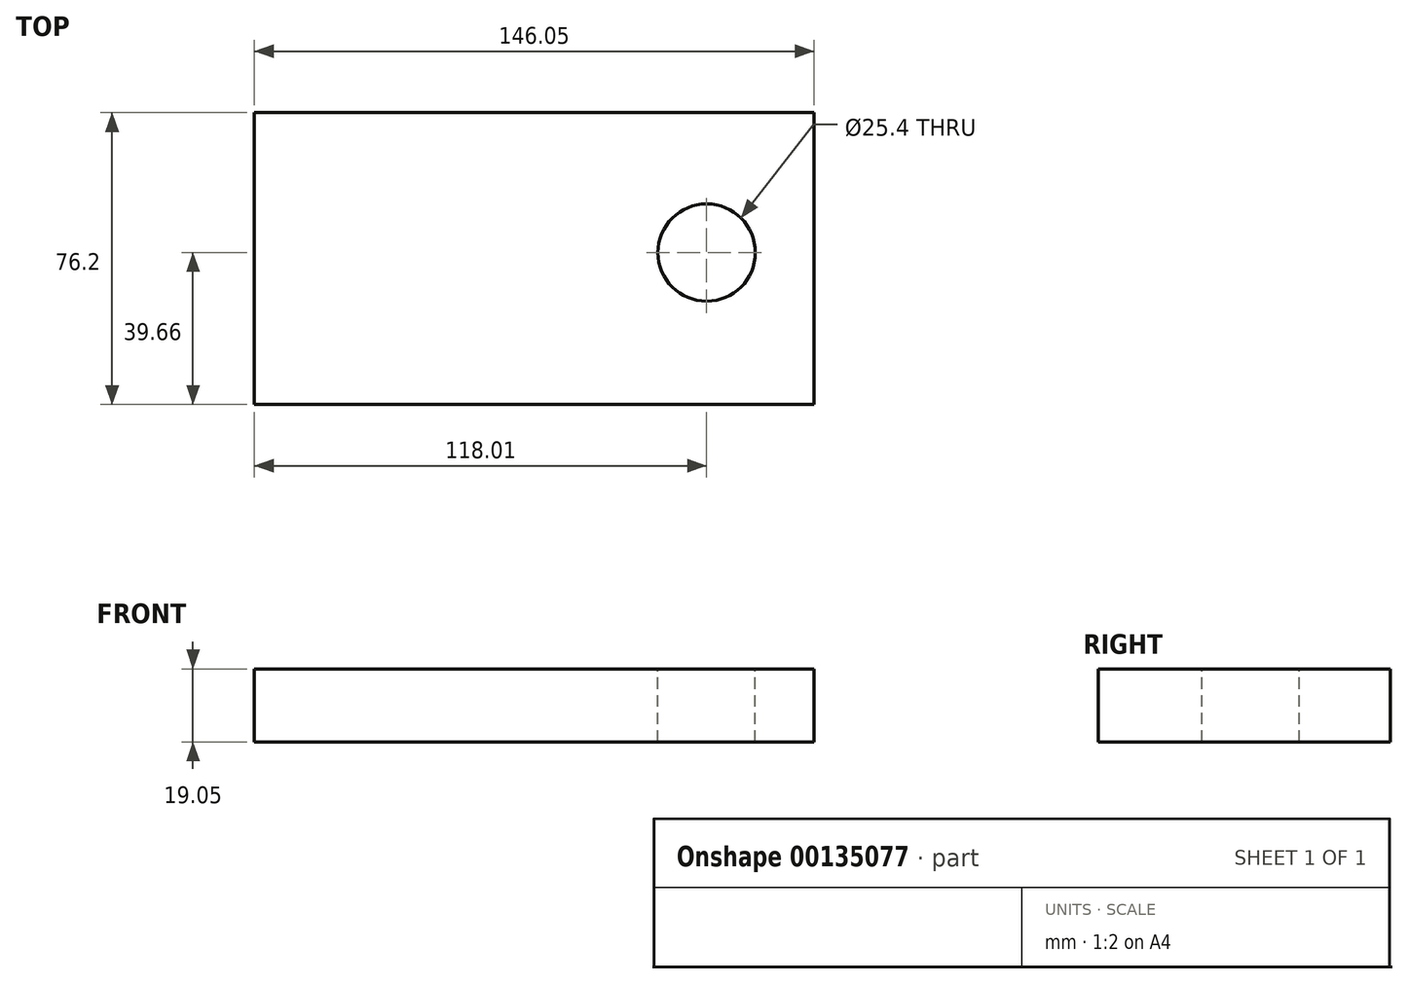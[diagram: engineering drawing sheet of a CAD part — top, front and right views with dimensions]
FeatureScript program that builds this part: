
annotation { "Feature Type Name" : "Feature", "Feature Type Description" : "" }
export const myFeature = defineFeature(function(context is Context, id is Id, definition is map)
    precondition{}
    {
        {
            var Q0;
            Q0=qCreatedBy(makeId("Top.planeOp"),FACE);
            var sketch = newSketch(context, id + "F0", { "sketchPlane" : qUnion([Q0])});
            skLineSegment(sketch, "E0.bottom", {"start": v(-70.58, 36.54) * mm, "end": v(75.47, 36.54) * mm});
            skLineSegment(sketch, "E0.top", {"start": v(-70.58, -39.66) * mm, "end": v(75.47, -39.66) * mm});
            skLineSegment(sketch, "E0.left", {"start": v(-70.58, 36.54) * mm, "end": v(-70.58, -39.66) * mm});
            skLineSegment(sketch, "E0.right", {"start": v(75.47, 36.54) * mm, "end": v(75.47, -39.66) * mm});
            skSolve(sketch);
        }
        {
            var Q0;
            Q0=makeQuery(id+"F0.imprint","IMPRINT",FACE,{"disambiguationData":[TD([[makeQuery(id+"F0.imprint","IMPRINT",EDGE,{"derivedFrom":sQuery(id+"F0.wireOp",EDGE,"E0.bottom")}),-1.0]])]});
            extrude(context, id + "F1", {"entities" : qUnion([Q0]), "depth" : 19.05 * mm});
        }
        {
            var Q0;
            Q0=makeQuery(id+"F1.opExtrude","CAP_FACE",FACE,{"disambiguationData":[OSD([sQuery(id+"F0.wireOp",EDGE,"E0.bottom"),sQuery(id+"F0.wireOp",EDGE,"E0.top"),sQuery(id+"F0.wireOp",EDGE,"E0.left"),sQuery(id+"F0.wireOp",EDGE,"E0.right")])],"isStart":false});
            var sketch = newSketch(context, id + "F2", { "sketchPlane" : qUnion([Q0])});
            skLineSegment(sketch, "E1.bottom", {"start": v(-58.81, 11.6) * mm, "end": v(-33.41, 11.6) * mm});
            skLineSegment(sketch, "E1.top", {"start": v(-58.81, -13.8) * mm, "end": v(-33.41, -13.8) * mm});
            skLineSegment(sketch, "E1.left", {"start": v(-58.81, 11.6) * mm, "end": v(-58.81, -13.8) * mm});
            skLineSegment(sketch, "E1.right", {"start": v(-33.41, 11.6) * mm, "end": v(-33.41, -13.8) * mm});
            skCircle(sketch, "E2", {"center": v(47.43, 0) * mm, "radius": 12.7 * mm});
            skLineSegment(sketch, "E3", {"start": v(0, 11.6) * mm, "end": v(-12.7, -10.4) * mm});
            skLineSegment(sketch, "E4", {"start": v(-12.7, -10.4) * mm, "end": v(12.7, -10.4) * mm});
            skLineSegment(sketch, "E5", {"start": v(12.7, -10.4) * mm, "end": v(0, 11.6) * mm});
            skSolve(sketch);
        }
        {
            var Q0;
            Q0=sQuery(id+"F2.wireOp",VERTEX,"E2.center");
            var Q1;
            Q1=makeQuery(id+"F1.opExtrude","SWEPT_BODY",BODY,{"disambiguationData":[OSD([sQuery(id+"F0.wireOp",EDGE,"E0.bottom"),sQuery(id+"F0.wireOp",EDGE,"E0.top"),sQuery(id+"F0.wireOp",EDGE,"E0.left"),sQuery(id+"F0.wireOp",EDGE,"E0.right")])]});
            hole(context, id + "F3", {"style" : HoleStyle.SIMPLE, "endStyle" : HoleEndStyle.THROUGH, "holeDiameter" : 25.4 * mm, "locations" : qUnion([Q0]), "scope" : qUnion([Q1]), "isTappedThrough" : true});
        }
    });
